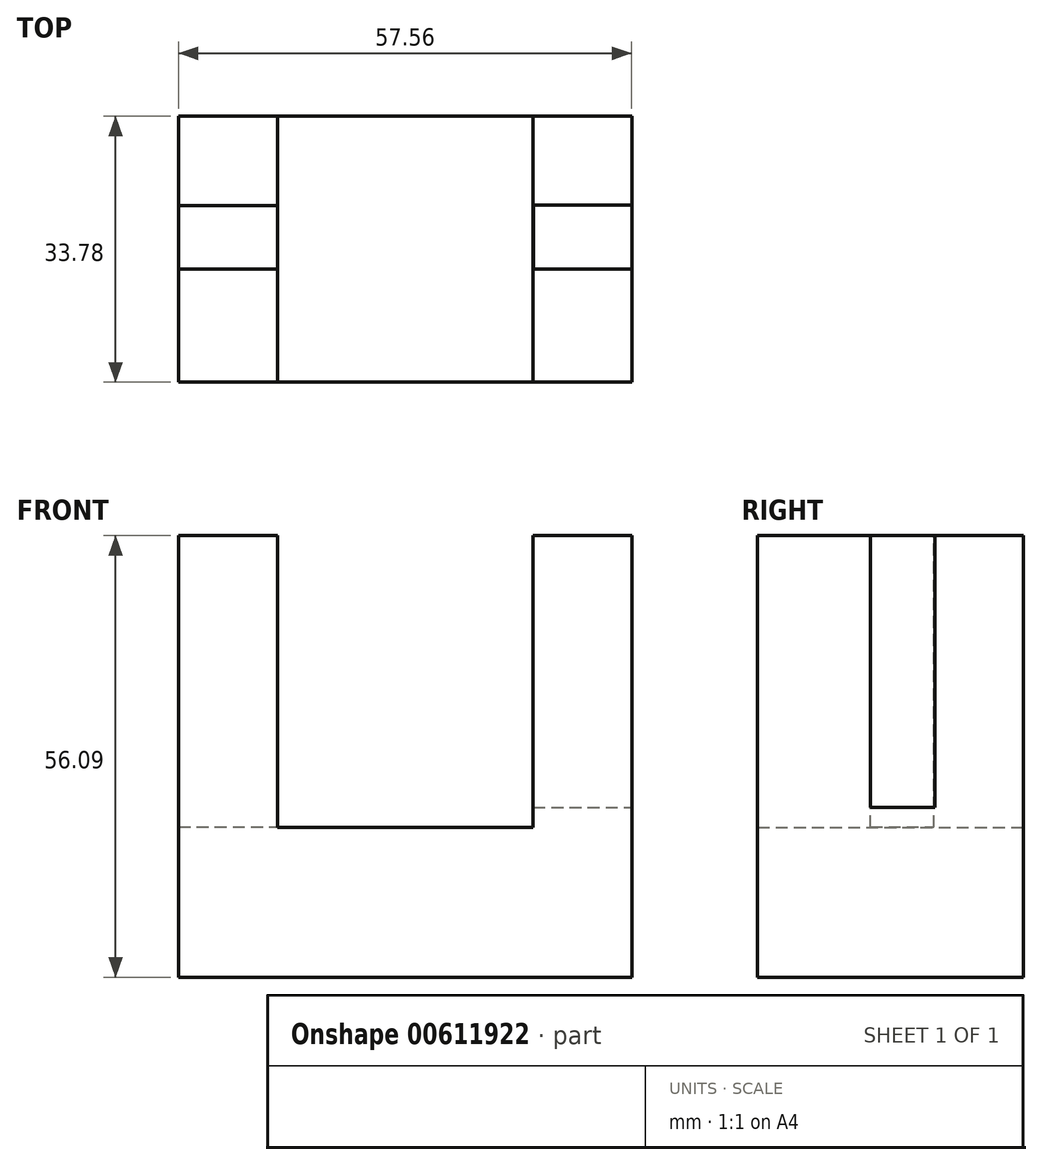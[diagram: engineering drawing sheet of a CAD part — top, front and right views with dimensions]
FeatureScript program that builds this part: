
annotation { "Feature Type Name" : "Feature", "Feature Type Description" : "" }
export const myFeature = defineFeature(function(context is Context, id is Id, definition is map)
    precondition{}
    {
        {
            var Q0;
            Q0=qCreatedBy(makeId("Front.planeOp"),FACE);
            var sketch = newSketch(context, id + "F0", { "sketchPlane" : qUnion([Q0])});
            skLineSegment(sketch, "E0.bottom", {"start": v(0, 0) * mm, "end": v(56.55, 0) * mm});
            skLineSegment(sketch, "E0.top", {"start": v(0, 56.09) * mm, "end": v(12.56, 56.09) * mm});
            skLineSegment(sketch, "E0.left", {"start": v(0, 0) * mm, "end": v(0, 56.09) * mm});
            skLineSegment(sketch, "E0.right", {"start": v(56.55, 0) * mm, "end": v(56.55, 56.09) * mm});
            skLineSegment(sketch, "E1.top", {"start": v(12.56, 19.06) * mm, "end": v(45, 19.06) * mm});
            skLineSegment(sketch, "E1.left", {"start": v(12.56, 56.09) * mm, "end": v(12.56, 19.06) * mm});
            skLineSegment(sketch, "E1.right", {"start": v(45, 56.09) * mm, "end": v(45, 19.06) * mm});
            skLineSegment(sketch, "E2.trimOffspring", {"start": v(45, 56.09) * mm, "end": v(56.55, 56.09) * mm});
            skSolve(sketch);
        }
        {
            var Q0;
            Q0 = qSketchRegion(id + "F0", true);
            extrude(context, id + "F1", {"entities" : qUnion([Q0]), "depth" : 33.78 * mm, "offsetDistance" : 25.4 * mm});
        }
        {
            var Q0;
            Q0=makeQuery(id+"F1.opExtrude","SWEPT_FACE",FACE,{"disambiguationData":[OSD([sQuery(id+"F0.wireOp",EDGE,"E0.right")])]});
            extrude(context, id + "F2", {"entities" : qUnion([Q0]), "operationType" : NewBodyOperationType.ADD, "depth" : 1.02 * mm, "offsetDistance" : 25.4 * mm});
        }
        {
            var Q0;
            Q0=makeQuery(id+"F1.opExtrude","SWEPT_FACE",FACE,{"disambiguationData":[OSD([sQuery(id+"F0.wireOp",EDGE,"E0.top")])]});
            var sketch = newSketch(context, id + "F3", { "sketchPlane" : qUnion([Q0])});
            skLineSegment(sketch, "E3.bottom", {"start": v(0, -19.43) * mm, "end": v(12.56, -19.43) * mm});
            skLineSegment(sketch, "E3.top", {"start": v(0, -11.36) * mm, "end": v(12.56, -11.36) * mm});
            skLineSegment(sketch, "E3.left", {"start": v(0, -19.43) * mm, "end": v(0, -11.36) * mm});
            skLineSegment(sketch, "E3.right", {"start": v(12.56, -19.43) * mm, "end": v(12.56, -11.36) * mm});
            skLineSegment(sketch, "E4.bottom", {"start": v(45.07, -19.43) * mm, "end": v(57.6, -19.43) * mm});
            skLineSegment(sketch, "E4.top", {"start": v(45.07, -11.25) * mm, "end": v(57.6, -11.25) * mm});
            skLineSegment(sketch, "E4.left", {"start": v(45.07, -19.43) * mm, "end": v(45.07, -11.25) * mm});
            skLineSegment(sketch, "E4.right", {"start": v(57.6, -19.43) * mm, "end": v(57.6, -11.25) * mm});
            skSolve(sketch);
        }
        {
            var Q0;
            Q0=makeQuery(id+"F3.imprint","IMPRINT",FACE,{"disambiguationData":[TD([[makeQuery(id+"F3.imprint","IMPRINT",EDGE,{"derivedFrom":sQuery(id+"F3.wireOp",EDGE,"E3.bottom")}),1.0]])]});
            extrude(context, id + "F4", {"entities" : qUnion([Q0]), "operationType" : NewBodyOperationType.REMOVE, "oppositeDirection" : true, "depth" : 37 * mm, "offsetDistance" : 25.4 * mm});
        }
        {
            var Q0;
            Q0 = qSketchRegion(id + "F3", true);
            extrude(context, id + "F5", {"entities" : qUnion([Q0]), "operationType" : NewBodyOperationType.REMOVE, "oppositeDirection" : true, "depth" : 34.54 * mm, "offsetDistance" : 25.4 * mm});
        }
    });
